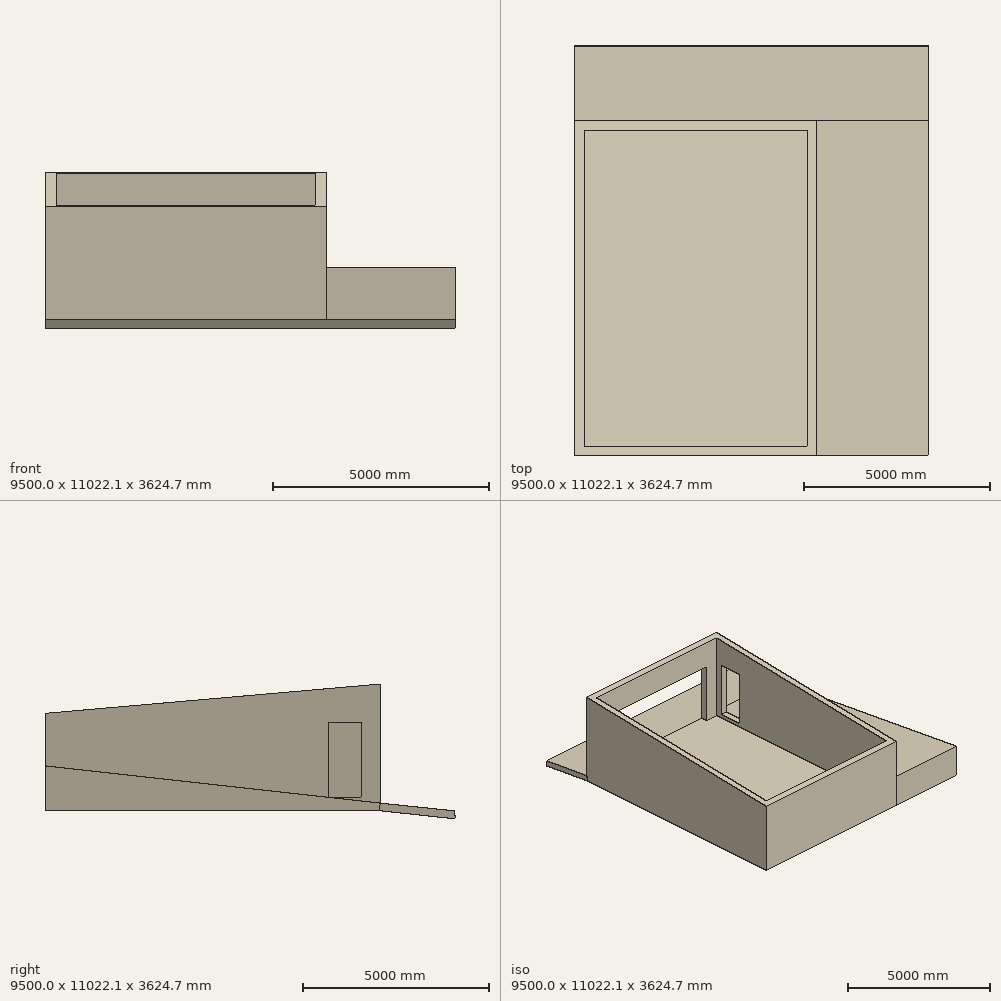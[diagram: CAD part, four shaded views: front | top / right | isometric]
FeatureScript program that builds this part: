
annotation { "Feature Type Name" : "Feature", "Feature Type Description" : "" }
export const myFeature = defineFeature(function(context is Context, id is Id, definition is map)
    precondition{}
    {
        {
            var Q0;
            Q0=qCreatedBy(makeId("Top.planeOp"),FACE);
            var sketch = newSketch(context, id + "F0", { "sketchPlane" : qUnion([Q0])});
            skLineSegment(sketch, "E0.bottom", {"start": v(3250, 4500) * mm, "end": v(-3250, 4500) * mm});
            skLineSegment(sketch, "E0.top", {"start": v(3250, -4500) * mm, "end": v(-3250, -4500) * mm});
            skLineSegment(sketch, "E0.left", {"start": v(3250, 4500) * mm, "end": v(3250, -4500) * mm});
            skLineSegment(sketch, "E0.right", {"start": v(-3250, 4500) * mm, "end": v(-3250, -4500) * mm});
            skPoint(sketch, "E0.middle", {"position": v(0, 0) * mm});
            skLineSegment(sketch, "E1.bottom", {"start": v(3000, 4250) * mm, "end": v(-3000, 4250) * mm});
            skLineSegment(sketch, "E1.top", {"start": v(3000, -4250) * mm, "end": v(-3000, -4250) * mm});
            skLineSegment(sketch, "E1.left", {"start": v(3000, 4250) * mm, "end": v(3000, -4250) * mm});
            skLineSegment(sketch, "E1.right", {"start": v(-3000, 4250) * mm, "end": v(-3000, -4250) * mm});
            skSolve(sketch);
        }
        {
            var Q0;
            Q0=makeQuery(id+"F0.imprint","IMPRINT",FACE,{"disambiguationData":[TD([[makeQuery(id+"F0.imprint","IMPRINT",EDGE,{"derivedFrom":sQuery(id+"F0.wireOp",EDGE,"E0.bottom")}),1.0]])]});
            extrude(context, id + "F1", {"entities" : qUnion([Q0]), "depth" : 3200 * mm});
        }
        {
            var Q0;
            Q0=makeQuery(id+"F1.opExtrude","SWEPT_FACE",FACE,{"disambiguationData":[OSD([sQuery(id+"F0.wireOp",EDGE,"E0.right")])]});
            var sketch = newSketch(context, id + "F2", { "sketchPlane" : qUnion([Q0])});
            skLineSegment(sketch, "E2", {"start": v(-4500, 3200) * mm, "end": v(4500, 2412.6) * mm});
            skLineSegment(sketch, "E3", {"start": v(4500, 2412.6) * mm, "end": v(4500, 3200) * mm});
            skLineSegment(sketch, "E4", {"start": v(4500, 3200) * mm, "end": v(-4500, 3200) * mm});
            skSolve(sketch);
        }
        {
            var Q0;
            Q0=makeQuery(id+"F2.imprint","IMPRINT",FACE,{"disambiguationData":[TD([[makeQuery(id+"F2.imprint","IMPRINT",EDGE,{"derivedFrom":sQuery(id+"F2.wireOp",EDGE,"E2")}),1.0]])]});
            extrude(context, id + "F3", {"entities" : qUnion([Q0]), "operationType" : NewBodyOperationType.REMOVE, "endBound" : BoundingType.THROUGH_ALL, "oppositeDirection" : true, "depth" : 25 * mm});
        }
        {
            var Q0;
            Q0=makeQuery(id+"F1.opExtrude","SWEPT_FACE",FACE,{"disambiguationData":[OSD([sQuery(id+"F0.wireOp",EDGE,"E0.bottom")])]});
            var sketch = newSketch(context, id + "F4", { "sketchPlane" : qUnion([Q0])});
            skLineSegment(sketch, "E5.bottom", {"start": v(2500, 2200) * mm, "end": v(-2500, 2200) * mm});
            skLineSegment(sketch, "E5.top", {"start": v(2500, 0) * mm, "end": v(-2500, 0) * mm});
            skLineSegment(sketch, "E5.left", {"start": v(2500, 2200) * mm, "end": v(2500, 0) * mm});
            skLineSegment(sketch, "E5.right", {"start": v(-2500, 2200) * mm, "end": v(-2500, 0) * mm});
            skSolve(sketch);
        }
        {
            var Q0;
            Q0 = qSketchRegion(id + "F4", true);
            extrude(context, id + "F5", {"entities" : qUnion([Q0]), "operationType" : NewBodyOperationType.REMOVE, "endBound" : BoundingType.UP_TO_NEXT, "oppositeDirection" : true, "depth" : 25 * mm});
        }
        {
            var Q0;
            Q0=makeQuery(id+"F1.opExtrude","CAP_FACE",FACE,{"disambiguationData":[OSD([sQuery(id+"F0.wireOp",EDGE,"E0.bottom"),sQuery(id+"F0.wireOp",EDGE,"E0.top"),sQuery(id+"F0.wireOp",EDGE,"E0.left"),sQuery(id+"F0.wireOp",EDGE,"E0.right"),sQuery(id+"F0.wireOp",EDGE,"E1.bottom"),sQuery(id+"F0.wireOp",EDGE,"E1.top"),sQuery(id+"F0.wireOp",EDGE,"E1.left"),sQuery(id+"F0.wireOp",EDGE,"E1.right")])],"isStart":true});
            var sketch = newSketch(context, id + "F6", { "sketchPlane" : qUnion([Q0])});
            skLineSegment(sketch, "E6.bottom", {"start": v(3250, 4500) * mm, "end": v(-3250, 4500) * mm});
            skLineSegment(sketch, "E6.top", {"start": v(3250, -4500) * mm, "end": v(-3250, -4500) * mm});
            skLineSegment(sketch, "E6.left", {"start": v(3250, 4500) * mm, "end": v(3250, -4500) * mm});
            skLineSegment(sketch, "E6.right", {"start": v(-3250, 4500) * mm, "end": v(-3250, -4500) * mm});
            skSolve(sketch);
        }
        {
            var Q0;
            Q0 = qSketchRegion(id + "F6", true);
            extrude(context, id + "F7", {"entities" : qUnion([Q0]), "operationType" : NewBodyOperationType.ADD, "depth" : 200 * mm});
        }
        {
            var Q0;
            Q0=makeQuery(id+"F7.boolean.opBoolean","MERGE",FACE,{"derivedFrom":[makeQuery(id+"F1.opExtrude","SWEPT_FACE",FACE,{"disambiguationData":[OSD([sQuery(id+"F0.wireOp",EDGE,"E0.left")])]}),makeQuery(id+"F7.opExtrude","SWEPT_FACE",FACE,{"disambiguationData":[OSD([sQuery(id+"F6.wireOp",EDGE,"E6.left")])]})]});
            var sketch = newSketch(context, id + "F8", { "sketchPlane" : qUnion([Q0])});
            skLineSegment(sketch, "E7", {"start": v(-4500, 1000) * mm, "end": v(4500, 0) * mm});
            skLineSegment(sketch, "E8", {"start": v(4500, 0) * mm, "end": v(4500, -200) * mm});
            skLineSegment(sketch, "E9", {"start": v(4500, -200) * mm, "end": v(-4500, -200) * mm});
            skLineSegment(sketch, "E10", {"start": v(-4500, -200) * mm, "end": v(-4500, 1000) * mm});
            skSolve(sketch);
        }
        {
            var Q0;
            Q0 = qSketchRegion(id + "F8", true);
            extrude(context, id + "F9", {"entities" : qUnion([Q0]), "depth" : 3000 * mm});
        }
        {
            var Q0;
            Q0=makeQuery(id+"F7.boolean.opBoolean","MERGE",FACE,{"derivedFrom":[makeQuery(id+"F1.opExtrude","SWEPT_FACE",FACE,{"disambiguationData":[OSD([sQuery(id+"F0.wireOp",EDGE,"E0.right")])]}),makeQuery(id+"F7.opExtrude","SWEPT_FACE",FACE,{"disambiguationData":[OSD([sQuery(id+"F6.wireOp",EDGE,"E6.right")])]})]});
            var sketch = newSketch(context, id + "F10", { "sketchPlane" : qUnion([Q0])});
            skLineSegment(sketch, "E11", {"start": v(-4475.48, -203.24) * mm, "end": v(-6522.09, -424.68) * mm});
            skLineSegment(sketch, "E12", {"start": v(-6522.09, -424.68) * mm, "end": v(-6493.52, -208.34) * mm});
            skLineSegment(sketch, "E13", {"start": v(-6493.52, -208.34) * mm, "end": v(-4500, 0) * mm});
            skLineSegment(sketch, "E14", {"start": v(-4500, 0) * mm, "end": v(-4475.48, -203.24) * mm});
            skSolve(sketch);
        }
        {
            var Q0;
            Q0 = qSketchRegion(id + "F10", true);
            var Q1;
            Q1=makeQuery(id+"F9.opExtrude","CAP_FACE",FACE,{"disambiguationData":[OSD([sQuery(id+"F8.wireOp",EDGE,"E7"),sQuery(id+"F8.wireOp",EDGE,"E8"),sQuery(id+"F8.wireOp",EDGE,"E9"),sQuery(id+"F8.wireOp",EDGE,"E10")])],"isStart":false});
            extrude(context, id + "F11", {"entities" : qUnion([Q0]), "endBound" : BoundingType.UP_TO_SURFACE, "oppositeDirection" : true, "endBoundEntityFace" : qUnion([Q1]), "depth" : 25 * mm});
        }
        {
            var Q0;
            Q0=makeQuery(id+"F7.boolean.opBoolean","MERGE",FACE,{"derivedFrom":[makeQuery(id+"F1.opExtrude","SWEPT_FACE",FACE,{"disambiguationData":[OSD([sQuery(id+"F0.wireOp",EDGE,"E0.left")])]}),makeQuery(id+"F7.opExtrude","SWEPT_FACE",FACE,{"disambiguationData":[OSD([sQuery(id+"F6.wireOp",EDGE,"E6.left")])]})]});
            var sketch = newSketch(context, id + "F12", { "sketchPlane" : qUnion([Q0])});
            skLineSegment(sketch, "E15.bottom", {"start": v(3100, 155.56) * mm, "end": v(4000, 155.56) * mm});
            skLineSegment(sketch, "E15.top", {"start": v(3100, 2155.56) * mm, "end": v(4000, 2155.56) * mm});
            skLineSegment(sketch, "E15.left", {"start": v(3100, 155.56) * mm, "end": v(3100, 2155.56) * mm});
            skLineSegment(sketch, "E15.right", {"start": v(4000, 155.56) * mm, "end": v(4000, 2155.56) * mm});
            skSolve(sketch);
        }
        {
            var Q0;
            Q0 = qSketchRegion(id + "F12", true);
            extrude(context, id + "F13", {"entities" : qUnion([Q0]), "operationType" : NewBodyOperationType.REMOVE, "endBound" : BoundingType.UP_TO_NEXT, "oppositeDirection" : true, "depth" : 25 * mm});
        }
    });
